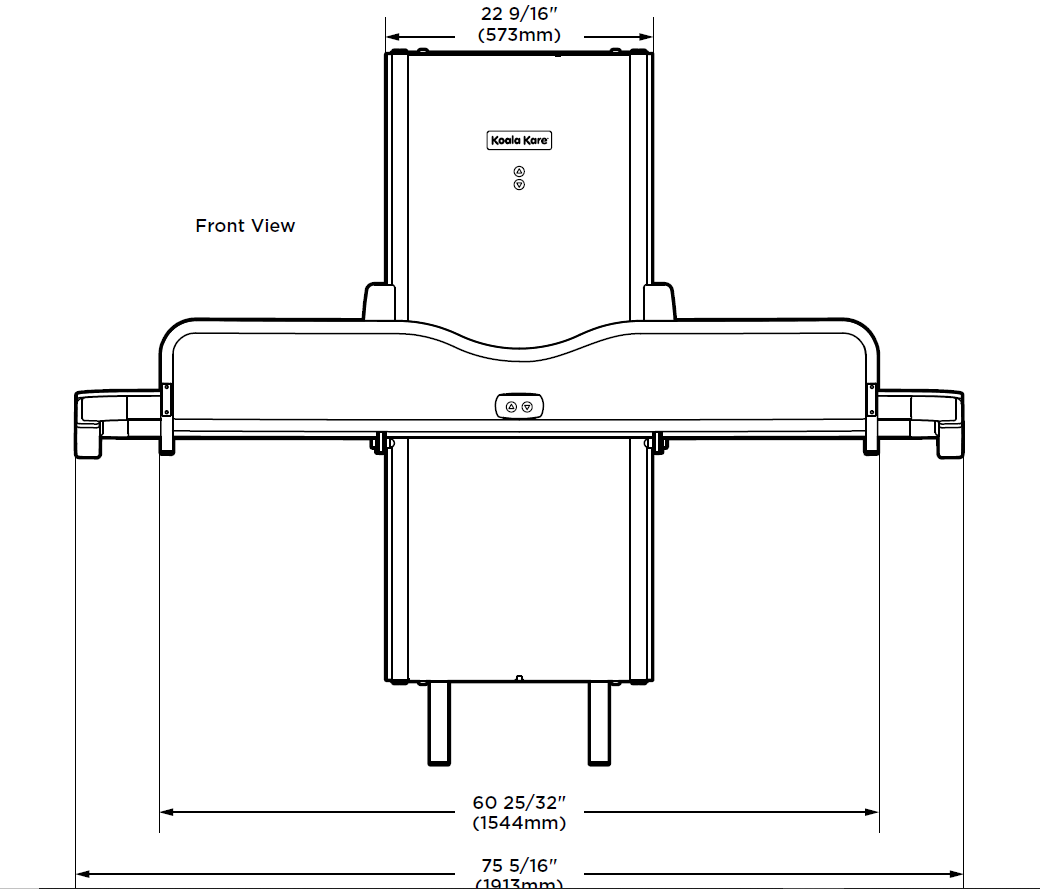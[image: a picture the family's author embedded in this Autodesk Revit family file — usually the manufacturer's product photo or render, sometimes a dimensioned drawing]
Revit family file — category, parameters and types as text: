
# Revit family: Changing_Station-Adjustable_Height-Koala_Kare-KB3000
name_source: partatom
category: Specialty Equipment
revit_build: Autodesk Revit 2018 (Build: 20170223_1515(x64)
units: mm (PartAtom-declared; Revit-internal decimal feet)

## family parameters
Cut with Voids When Loaded = No
Host = Face
OmniClass Number = 23.40.20.21
OmniClass Title = Toilet and Bath Specialties
Part Type = Normal
Room Calculation Point = No
Round Connector Dimension = Use Diameter
Shared = Yes

## types (1)
- KB3000
    Assembly Code = E2010
    Body Material = Metal-Koala_Kare-Stainless_Steel-Powder_Coated
    Default Elevation = 0"
    Description = Adjustable Height Changing Station
    Height = 60 15/32"
    Installation Type = Wall Mounted
    Length = 75 5/16"
    Manufacturer = Koala Kare
    Model = KB3000
    Price = Prices may vary. Please consult Manufacturer Representative for most up-to-date price list.
    Product Page URL = https://www.koalabear.com
    Type Comments = Adjustable height changing station shall have cut resistant single piece UHMW PE bed surface, attached to continuous 2" (50mm) 
square powder costed steel frame and integrated adjustable front guard. Front guard will be operable with one hand and lock in the 
up and down positions. Changing station shall have two integrated controls to be electronically height adjustable from 12" (300mm) 
- 41" (1040mm) and will have a fail-safe battery backup to prevent against unit failure during power outage. All moving parts shall be 
concealed or guarded in such way at to protect against pinch points or entrapment. The changing station shall be designed to support 
a load of up to 500lbs, with a changing surface that hammocks to provide optimal comfort to the occupant. Bed surface shall be cut 
resistant and field replaceable, with tamper resistant fasteners to connect it to the steel frame. Changing surface shall be no less than 75 
¼" (1911mm) x 31 ½" (800mm). Changing station shall be tested to meet IK10 Rating and shall have no exposed wiring/cables. Changing 
station shall be designed so that it can be hosed down for cleaning and can be used in wet room environment without compromising 
electronics
    URL = https://www.koalabear.com
    Width = 40 9/32"

## geometry (parser evidence)
native form markers: Sweep x2
no freeform markers — native parametric forms only
